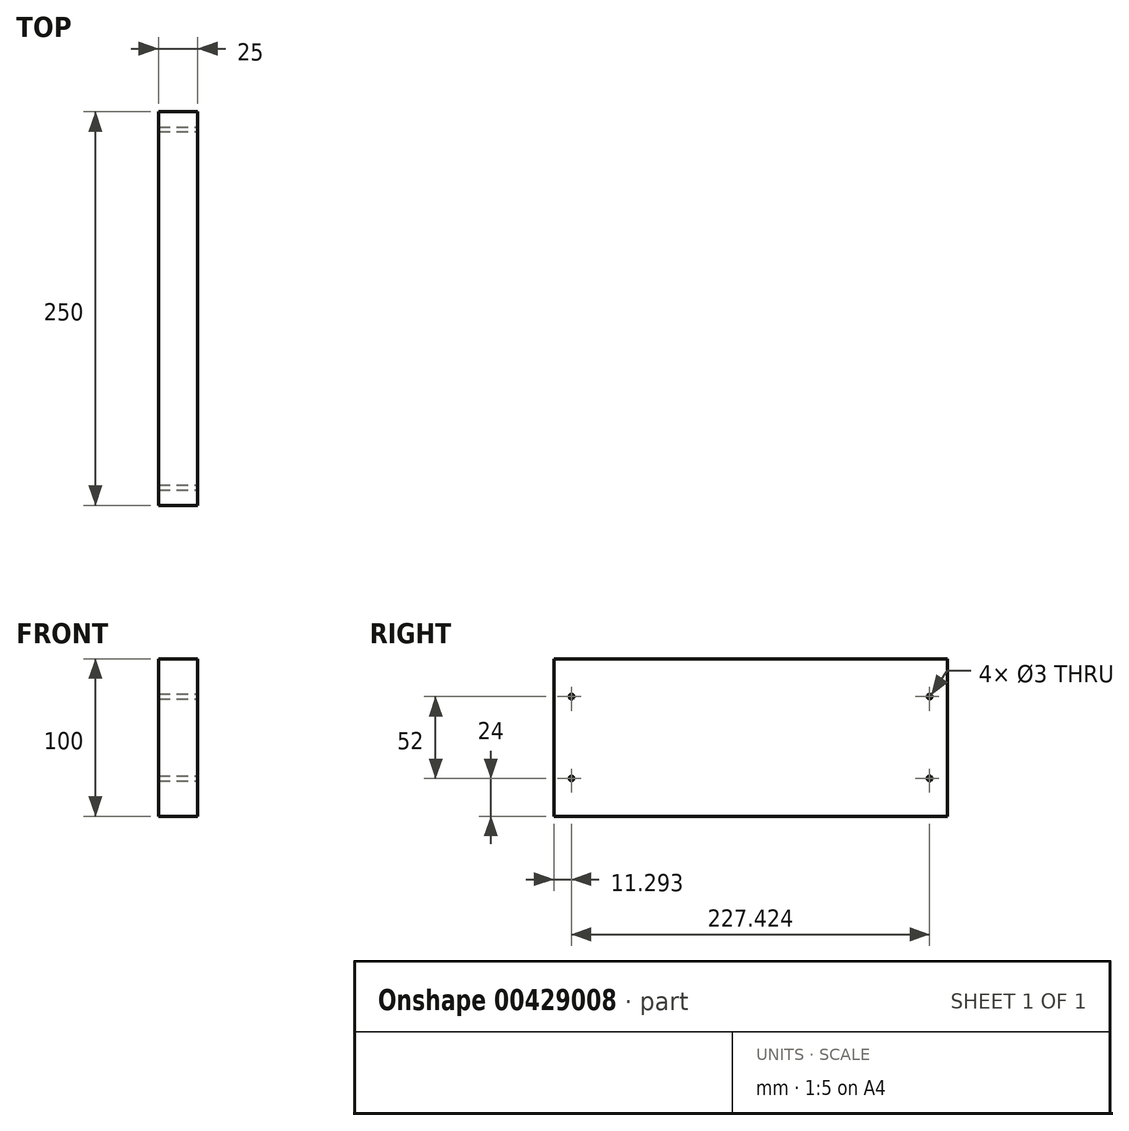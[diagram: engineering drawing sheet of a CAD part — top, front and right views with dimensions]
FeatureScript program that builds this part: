
annotation { "Feature Type Name" : "Feature", "Feature Type Description" : "" }
export const myFeature = defineFeature(function(context is Context, id is Id, definition is map)
    precondition{}
    {
        {
            var Q0;
            Q0=qCreatedBy(makeId("Right.planeOp"),FACE);
            var sketch = newSketch(context, id + "F0", { "sketchPlane" : qUnion([Q0])});
            skLineSegment(sketch, "E0.bottom", {"start": v(108.33, 0) * mm, "end": v(-141.67, 0) * mm});
            skLineSegment(sketch, "E0.top", {"start": v(108.33, 100) * mm, "end": v(-141.67, 100) * mm});
            skLineSegment(sketch, "E0.left", {"start": v(108.33, 0) * mm, "end": v(108.33, 100) * mm});
            skLineSegment(sketch, "E0.right", {"start": v(-141.67, 0) * mm, "end": v(-141.67, 100) * mm});
            skSolve(sketch);
        }
        {
            var Q0;
            Q0=makeQuery(id+"F0.imprint","IMPRINT",FACE,{"disambiguationData":[TD([[makeQuery(id+"F0.imprint","IMPRINT",EDGE,{"derivedFrom":sQuery(id+"F0.wireOp",EDGE,"E0.bottom")}),-1.0]])]});
            extrude(context, id + "F1", {"entities" : qUnion([Q0]), "depth" : 25 * mm});
        }
        {
            var Q0;
            Q0=makeQuery(id+"F1.opExtrude","CAP_FACE",FACE,{"disambiguationData":[OSD([sQuery(id+"F0.wireOp",EDGE,"E0.bottom"),sQuery(id+"F0.wireOp",EDGE,"E0.top"),sQuery(id+"F0.wireOp",EDGE,"E0.left"),sQuery(id+"F0.wireOp",EDGE,"E0.right")])],"isStart":false});
            var sketch = newSketch(context, id + "F2", { "sketchPlane" : qUnion([Q0])});
            skCircle(sketch, "E1", {"center": v(-130.38, 76) * mm, "radius": 1.5 * mm});
            skCircle(sketch, "E2.MirrorC", {"center": v(97.05, 76) * mm, "radius": 1.5 * mm});
            skCircle(sketch, "E3.MirrorC", {"center": v(-130.38, 24) * mm, "radius": 1.5 * mm});
            skCircle(sketch, "E4.MirrorC", {"center": v(97.05, 24) * mm, "radius": 1.5 * mm});
            skSolve(sketch);
        }
        {
            var Q0;
            Q0=sQuery(id+"F2.wireOp",VERTEX,"E1.center");
            var Q1;
            Q1=sQuery(id+"F2.wireOp",VERTEX,"E3.MirrorC.center");
            var Q2;
            Q2=sQuery(id+"F2.wireOp",VERTEX,"E2.MirrorC.center");
            var Q3;
            Q3=sQuery(id+"F2.wireOp",VERTEX,"E4.MirrorC.center");
            var Q4;
            Q4=makeQuery(id+"F1.opExtrude","SWEPT_BODY",BODY,{"disambiguationData":[OSD([sQuery(id+"F0.wireOp",EDGE,"E0.bottom"),sQuery(id+"F0.wireOp",EDGE,"E0.top"),sQuery(id+"F0.wireOp",EDGE,"E0.left"),sQuery(id+"F0.wireOp",EDGE,"E0.right")])]});
            hole(context, id + "F3", {"style" : HoleStyle.SIMPLE, "endStyle" : HoleEndStyle.THROUGH, "holeDiameter" : 3 * mm, "isTappedThrough" : true, "tappedDepth" : 12 * mm, "tapClearance" : 3, "startFromSketch" : true, "locations" : qUnion([Q0, Q1, Q2, Q3]), "scope" : qUnion([Q4])});
        }
    });
